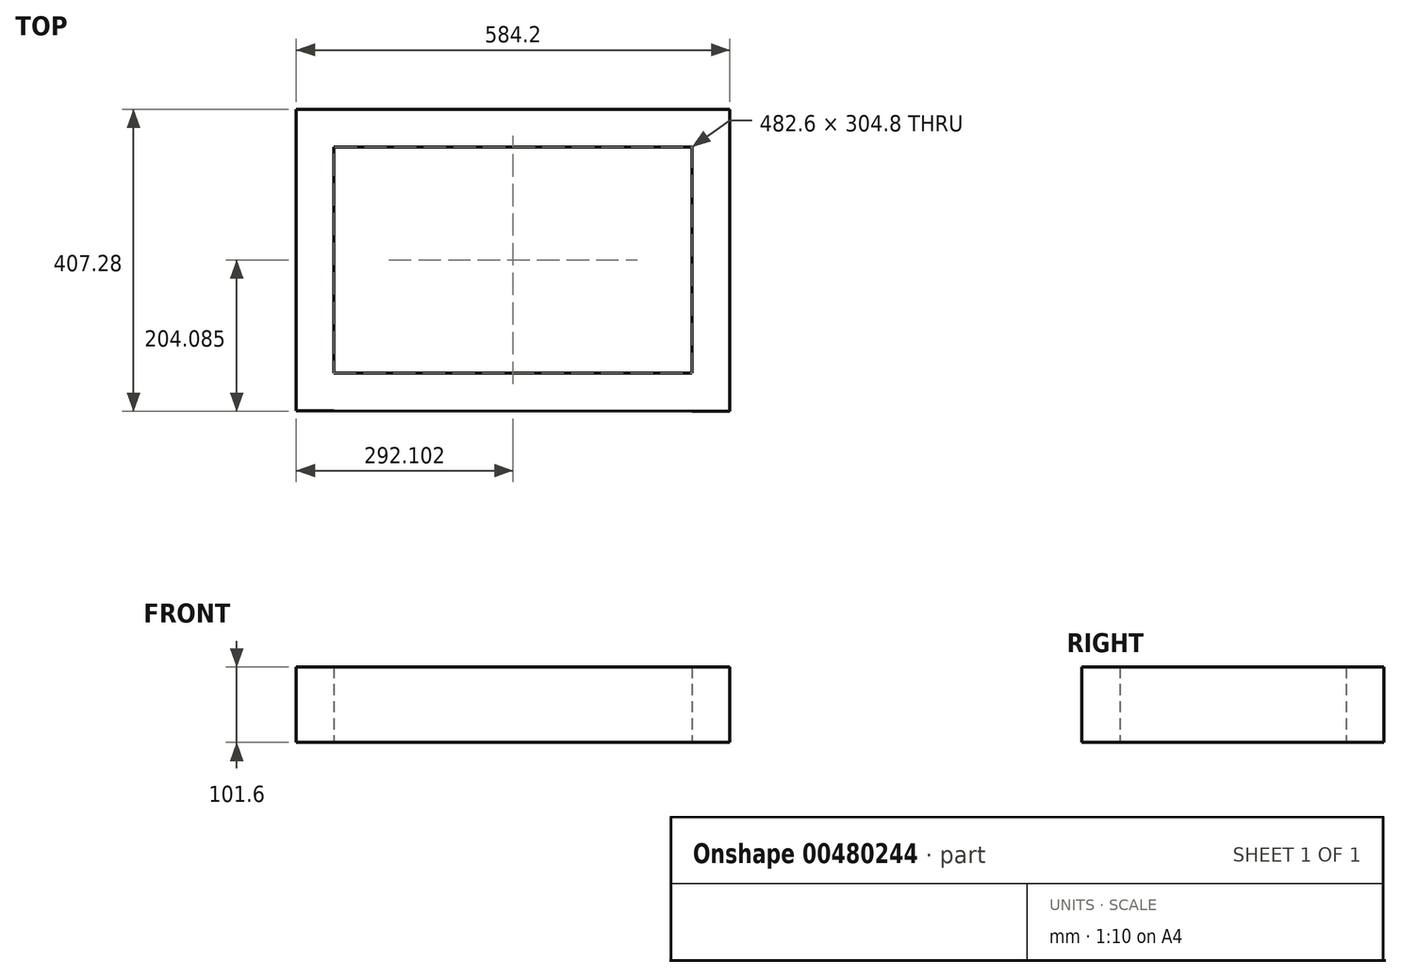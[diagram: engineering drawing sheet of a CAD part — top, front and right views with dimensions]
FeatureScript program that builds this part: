
annotation { "Feature Type Name" : "Feature", "Feature Type Description" : "" }
export const myFeature = defineFeature(function(context is Context, id is Id, definition is map)
    precondition{}
    {
        {
            var Q0;
            Q0=qCreatedBy(makeId("Top.planeOp"),FACE);
            var sketch = newSketch(context, id + "F0", { "sketchPlane" : qUnion([Q0])});
            skLineSegment(sketch, "E0.bottom", {"start": v(-110.73, 152.17) * mm, "end": v(16.27, 152.17) * mm});
            skLineSegment(sketch, "E0.top", {"start": v(-110.73, -152.63) * mm, "end": v(16.27, -152.63) * mm});
            skLineSegment(sketch, "E0.left", {"start": v(-110.73, 152.17) * mm, "end": v(-110.73, -152.63) * mm});
            skLineSegment(sketch, "E0.right", {"start": v(16.27, 152.17) * mm, "end": v(16.27, -152.63) * mm});
            skLineSegment(sketch, "E1.bottom", {"start": v(244.87, 152.17) * mm, "end": v(371.87, 152.17) * mm});
            skLineSegment(sketch, "E1.left", {"start": v(244.87, 152.17) * mm, "end": v(244.87, -152.63) * mm});
            skLineSegment(sketch, "E1.right", {"start": v(371.87, 152.17) * mm, "end": v(371.87, -152.63) * mm});
            skLineSegment(sketch, "E2", {"start": v(16.27, 152.17) * mm, "end": v(244.87, 152.17) * mm});
            skLineSegment(sketch, "E3", {"start": v(16.27, -152.63) * mm, "end": v(244.87, -152.63) * mm});
            skLineSegment(sketch, "E4.bottom", {"start": v(-110.73, 152.17) * mm, "end": v(371.87, 152.17) * mm});
            skLineSegment(sketch, "E4.top", {"start": v(-110.73, 202.97) * mm, "end": v(371.87, 202.97) * mm});
            skLineSegment(sketch, "E4.left", {"start": v(-110.73, 152.17) * mm, "end": v(-110.73, 202.97) * mm});
            skLineSegment(sketch, "E4.right", {"start": v(371.87, 152.17) * mm, "end": v(371.87, 202.97) * mm});
            skLineSegment(sketch, "E5.bottom", {"start": v(-110.73, 202.97) * mm, "end": v(-161.53, 202.97) * mm});
            skLineSegment(sketch, "E5.left", {"start": v(-110.73, 202.97) * mm, "end": v(-110.73, -152.63) * mm});
            skLineSegment(sketch, "E5.right", {"start": v(-161.53, 202.97) * mm, "end": v(-161.53, -152.63) * mm});
            skLineSegment(sketch, "E6.bottom", {"start": v(-110.73, -152.63) * mm, "end": v(244.87, -152.63) * mm});
            skLineSegment(sketch, "E6.top", {"start": v(-161.53, -203.43) * mm, "end": v(-110.73, -203.43) * mm});
            skLineSegment(sketch, "E6.left", {"start": v(-161.53, -152.63) * mm, "end": v(-161.53, -203.43) * mm});
            skLineSegment(sketch, "E7.bottom", {"start": v(371.87, 202.97) * mm, "end": v(422.67, 202.97) * mm});
            skLineSegment(sketch, "E7.top", {"start": v(371.87, -204.31) * mm, "end": v(422.67, -204.31) * mm});
            skLineSegment(sketch, "E7.left", {"start": v(371.87, 202.97) * mm, "end": v(371.87, -204.31) * mm});
            skLineSegment(sketch, "E7.right", {"start": v(422.67, 202.97) * mm, "end": v(422.67, -204.31) * mm});
            skLineSegment(sketch, "E8", {"start": v(-110.73, -152.63) * mm, "end": v(-110.73, -203.43) * mm});
            skLineSegment(sketch, "E9.bottom", {"start": v(16.27, 152.17) * mm, "end": v(67.07, 152.17) * mm});
            skLineSegment(sketch, "E9.top", {"start": v(16.27, -152.63) * mm, "end": v(67.07, -152.63) * mm});
            skLineSegment(sketch, "E9.right", {"start": v(67.07, 152.17) * mm, "end": v(67.07, -152.63) * mm});
            skLineSegment(sketch, "E10.bottom", {"start": v(244.87, 152.17) * mm, "end": v(194.07, 152.17) * mm});
            skLineSegment(sketch, "E10.top", {"start": v(244.87, -152.63) * mm, "end": v(194.07, -152.63) * mm});
            skLineSegment(sketch, "E10.right", {"start": v(194.07, 152.17) * mm, "end": v(194.07, -152.63) * mm});
            skLineSegment(sketch, "E11", {"start": v(244.87, -152.63) * mm, "end": v(371.87, -152.63) * mm});
            skLineSegment(sketch, "E12", {"start": v(371.87, -204.31) * mm, "end": v(-110.73, -203.43) * mm});
            skSolve(sketch);
        }
        {
            var Q0;
            {var subQ3=sQuery(id+"F0.wireOp",EDGE,"E7.bottom");Q0=makeQuery(id+"F0.imprint","IMPRINT",FACE,{"disambiguationData":[TD([[makeQuery(id+"F0.imprint","IMPRINT",EDGE,{"derivedFrom":subQ3}),-1.0]])]});}
            var Q1;
            {var subQ3=sQuery(id+"F0.wireOp",EDGE,"E5.bottom");Q1=makeQuery(id+"F0.imprint","IMPRINT",FACE,{"disambiguationData":[TD([[makeQuery(id+"F0.imprint","IMPRINT",EDGE,{"derivedFrom":subQ3}),1.0]])]});}
            var Q2;
            {var subQ0=sQuery(id+"F0.wireOp",EDGE,"E6.right");Q2=makeQuery(id+"F0.imprint","IMPRINT",FACE,{"disambiguationData":[TD([[makeQuery(id+"F0.imprint","IMPRINT",EDGE,{"derivedFrom":subQ0}),-1.0]])]});}
            var Q3;
            {var subQ8=sQuery(id+"F0.wireOp",EDGE,"E4.top");Q3=makeQuery(id+"F0.imprint","IMPRINT",FACE,{"disambiguationData":[TD([[makeQuery(id+"F0.imprint","IMPRINT",EDGE,{"derivedFrom":subQ8}),-1.0]])]});}
            var Q4;
            Q4=makeQuery(id+"F0.imprint","IMPRINT",FACE,{"disambiguationData":[TD([[makeQuery(id+"F0.imprint","IMPRINT",EDGE,{"derivedFrom":sQuery(id+"F0.wireOp",EDGE,"E9.bottom")}),-1.0]])]});
            var Q5;
            Q5=makeQuery(id+"F0.imprint","IMPRINT",FACE,{"disambiguationData":[TD([[makeQuery(id+"F0.imprint","IMPRINT",EDGE,{"derivedFrom":sQuery(id+"F0.wireOp",EDGE,"E10.bottom")}),1.0]])]});
            var Q6;
            {var subQ3=sQuery(id+"F0.wireOp",EDGE,"E1.right");Q6=makeQuery(id+"F0.imprint","IMPRINT",FACE,{"disambiguationData":[TD([[makeQuery(id+"F0.imprint","IMPRINT",EDGE,{"derivedFrom":subQ3}),1.0]])]});}
            var Q7;
            {var subQ6=sQuery(id+"F0.wireOp",EDGE,"E8");Q7=makeQuery(id+"F0.imprint","IMPRINT",FACE,{"disambiguationData":[TD([[makeQuery(id+"F0.imprint","IMPRINT",EDGE,{"derivedFrom":subQ6}),1.0]])]});}
            extrude(context, id + "F1", {"entities" : qUnion([Q0, Q1, Q2, Q3, Q4, Q5, Q6, Q7]), "depth" : 101.6 * mm, "offsetDistance" : 25.4 * mm});
        }
    });
